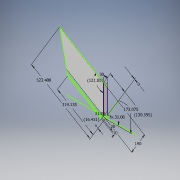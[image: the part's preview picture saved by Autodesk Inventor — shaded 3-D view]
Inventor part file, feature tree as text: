
AUTODESK INVENTOR PART (.ipt)
format: ipt  version: 2019 (Build 230136000, 136)  size: 207,360 bytes
history: native  units: mm
features: sheet_metal_op x4, sketch x2, other x1
ambient origin geometry x8: Origin, YZ Plane, XZ Plane, XY Plane, X Axis, Y Axis, Z Axis, Center Point
bodies: Solid1 (feature_tree)
feature tree (7):
  sketch  "Sketch1"  dims[d0=5.410521mm]
  sheet_metal_op  "Face1"
  sheet_metal_op  "Fold13"
  sheet_metal_op  "Hem1"
  sheet_metal_op  "Fold15"
  other  "Plate1"
  sketch  "Sketch3"  dims[d6=5.410521mm d7=30.0mm d8=0.5mm d86=0.5mm d87=0.25mm d88=1.0mm d89=0.5mm d90=60.0deg d91=0.5mm d92=21.118484mm d93=0.0mm d94=0.5mm d95=0.25mm d96=1.0mm d97=0.5mm d98=2.0mm d99=0.25mm d100=0.125mm d108=16.431036mm d111=319.134943mm d112=523.407815mm d114=130.594554mm d116=20.0mm d117=10.0mm d118=190.0mm d119=173.074754mm d120=0.5mm d121=0.25mm d122=1.0mm d123=0.5mm d124=90.0deg d125=2.0mm]
